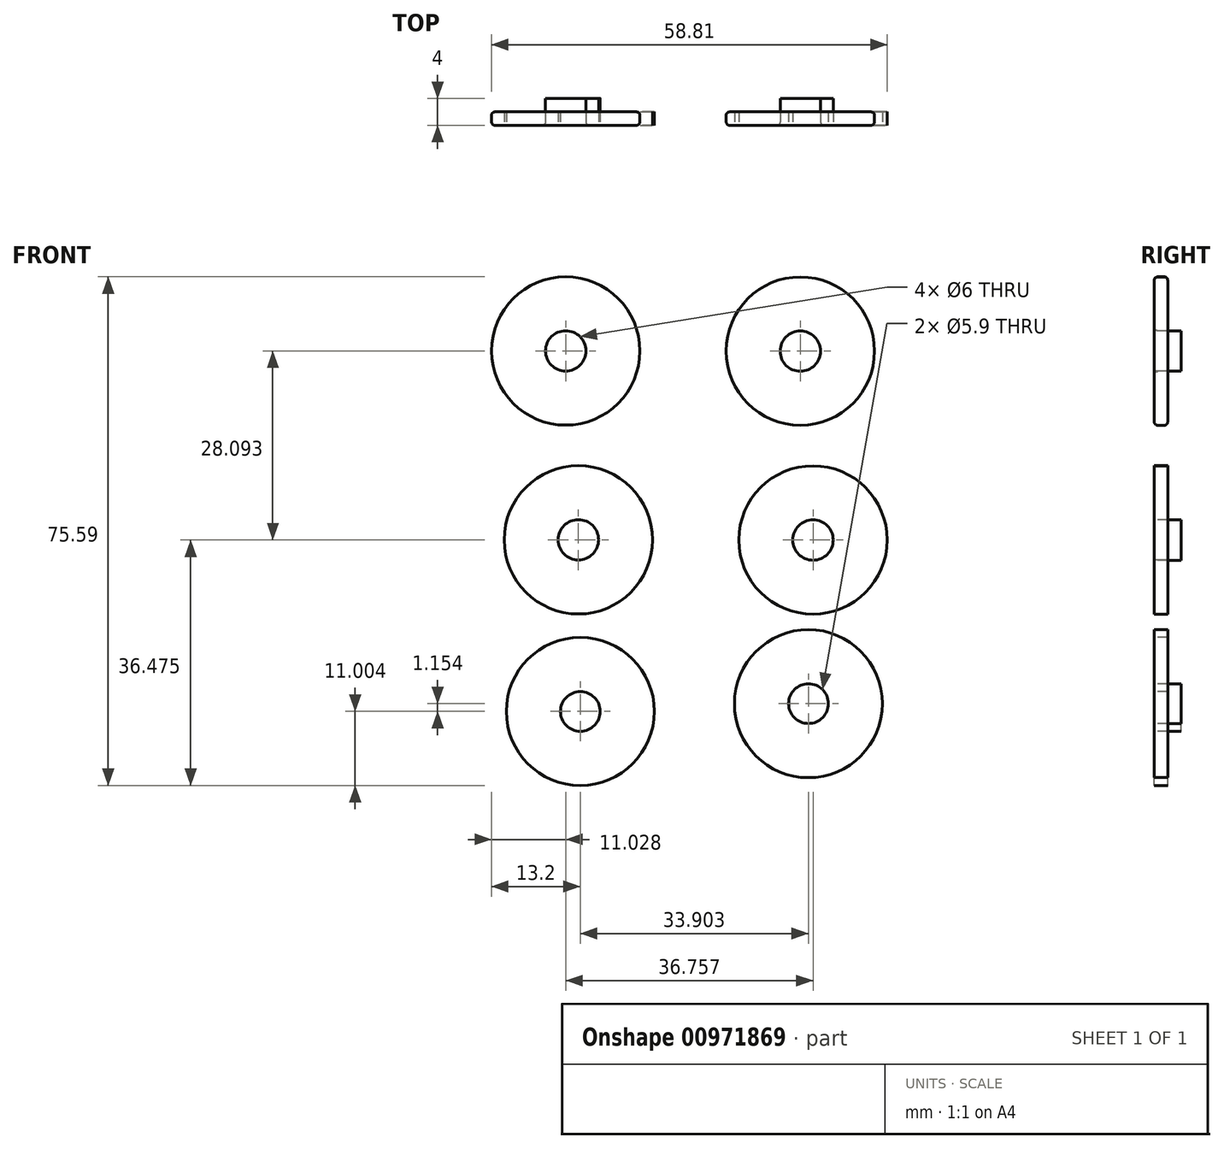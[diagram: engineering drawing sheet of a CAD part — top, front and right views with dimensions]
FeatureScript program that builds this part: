
annotation { "Feature Type Name" : "Feature", "Feature Type Description" : "" }
export const myFeature = defineFeature(function(context is Context, id is Id, definition is map)
    precondition{}
    {
        {
            var Q0;
            Q0=qCreatedBy(makeId("Front.planeOp"),FACE);
            var sketch = newSketch(context, id + "F0", { "sketchPlane" : qUnion([Q0])});
            skCircle(sketch, "E0", {"center": v(-13.67, 28.07) * mm, "radius": 11.03 * mm});
            skCircle(sketch, "E1", {"center": v(21.2, 28.04) * mm, "radius": 11.03 * mm});
            skCircle(sketch, "E2", {"center": v(-13.67, 28.07) * mm, "radius": 3 * mm});
            skCircle(sketch, "E3", {"center": v(21.2, 28.04) * mm, "radius": 3 * mm});
            skCircle(sketch, "E4", {"center": v(-11.79, 0) * mm, "radius": 11.03 * mm});
            skCircle(sketch, "E5", {"center": v(23.08, -0.02) * mm, "radius": 11.03 * mm});
            skCircle(sketch, "E6", {"center": v(-11.79, 0) * mm, "radius": 3 * mm});
            skCircle(sketch, "E7", {"center": v(23.08, -0.02) * mm, "radius": 3 * mm});
            skSolve(sketch);
        }
        {
            var Q0;
            Q0=makeQuery(id+"F0.imprint","IMPRINT",FACE,{"disambiguationData":[TD([[makeQuery(id+"F0.imprint","IMPRINT",EDGE,{"derivedFrom":sQuery(id+"F0.wireOp",EDGE,"E1")}),1.0]])]});
            var Q1;
            Q1=makeQuery(id+"F0.imprint","IMPRINT",FACE,{"disambiguationData":[TD([[makeQuery(id+"F0.imprint","IMPRINT",EDGE,{"derivedFrom":sQuery(id+"F0.wireOp",EDGE,"E0")}),1.0]])]});
            extrude(context, id + "F1", {"entities" : qUnion([Q0, Q1]), "depth" : -2 * mm, "offsetDistance" : 25.4 * mm});
        }
        {
            var Q0;
            Q0=makeQuery(id+"F1.opExtrude","CAP_EDGE",EDGE,{"disambiguationData":[OSD([sQuery(id+"F0.wireOp",EDGE,"E1")])],"isStart":false});
            var Q1;
            Q1=makeQuery(id+"F1.opExtrude","CAP_EDGE",EDGE,{"disambiguationData":[OSD([sQuery(id+"F0.wireOp",EDGE,"E0")])],"isStart":false});
            fillet(context, id + "F2", {"entities" : qUnion([Q0, Q1]), "radius" : .5 * mm, "tangentPropagation" : true, "allowEdgeOverflow" : false});
        }
        {
            var Q0;
            Q0=makeQuery(id+"F0.imprint","IMPRINT",FACE,{"disambiguationData":[TD([[makeQuery(id+"F0.imprint","IMPRINT",EDGE,{"derivedFrom":sQuery(id+"F0.wireOp",EDGE,"E2")}),1.0]])]});
            var Q1;
            Q1=makeQuery(id+"F0.imprint","IMPRINT",FACE,{"disambiguationData":[TD([[makeQuery(id+"F0.imprint","IMPRINT",EDGE,{"derivedFrom":sQuery(id+"F0.wireOp",EDGE,"E3")}),1.0]])]});
            extrude(context, id + "F3", {"entities" : qUnion([Q0, Q1]), "depth" : -4 * mm, "offsetDistance" : 25.4 * mm});
        }
        {
            var Q0;
            Q0=makeQuery(id+"F1.opExtrude","CAP_FACE",FACE,{"disambiguationData":[OSD([sQuery(id+"F0.wireOp",EDGE,"E0"),sQuery(id+"F0.wireOp",EDGE,"E2")])],"isStart":true});
            var Q1;
            Q1=makeQuery(id+"F1.opExtrude","CAP_FACE",FACE,{"disambiguationData":[OSD([sQuery(id+"F0.wireOp",EDGE,"E1"),sQuery(id+"F0.wireOp",EDGE,"E3")])],"isStart":true});
            fillet(context, id + "F4", {"entities" : qUnion([Q0, Q1]), "radius" : .55 * mm, "tangentPropagation" : true, "allowEdgeOverflow" : false});
        }
        {
            var Q0;
            Q0=makeQuery(id+"F0.imprint","IMPRINT",FACE,{"disambiguationData":[TD([[makeQuery(id+"F0.imprint","IMPRINT",EDGE,{"derivedFrom":sQuery(id+"F0.wireOp",EDGE,"E4")}),1.0]])]});
            var Q1;
            Q1=makeQuery(id+"F0.imprint","IMPRINT",FACE,{"disambiguationData":[TD([[makeQuery(id+"F0.imprint","IMPRINT",EDGE,{"derivedFrom":sQuery(id+"F0.wireOp",EDGE,"E5")}),1.0]])]});
            extrude(context, id + "F5", {"entities" : qUnion([Q0, Q1]), "depth" : -2 * mm, "offsetDistance" : 25 * mm});
        }
        {
            var Q0;
            Q0=makeQuery(id+"F0.imprint","IMPRINT",FACE,{"disambiguationData":[TD([[makeQuery(id+"F0.imprint","IMPRINT",EDGE,{"derivedFrom":sQuery(id+"F0.wireOp",EDGE,"E6")}),1.0]])]});
            var Q1;
            Q1=makeQuery(id+"F0.imprint","IMPRINT",FACE,{"disambiguationData":[TD([[makeQuery(id+"F0.imprint","IMPRINT",EDGE,{"derivedFrom":sQuery(id+"F0.wireOp",EDGE,"E7")}),1.0]])]});
            extrude(context, id + "F6", {"entities" : qUnion([Q0, Q1]), "depth" : -4 * mm, "offsetDistance" : 25 * mm});
        }
        {
            var Q0;
            Q0=qCreatedBy(makeId("Front.planeOp"),FACE);
            var sketch = newSketch(context, id + "F7", { "sketchPlane" : qUnion([Q0])});
            skCircle(sketch, "E8", {"center": v(22.4, -24.34) * mm, "radius": 11 * mm});
            skCircle(sketch, "E9", {"center": v(22.4, -24.34) * mm, "radius": 2.95 * mm});
            skCircle(sketch, "E10", {"center": v(-11.5, -25.5) * mm, "radius": 11 * mm});
            skCircle(sketch, "E11", {"center": v(-11.5, -25.5) * mm, "radius": 2.95 * mm});
            skSolve(sketch);
        }
        {
            var Q0;
            Q0=makeQuery(id+"F7.imprint","IMPRINT",FACE,{"disambiguationData":[TD([[makeQuery(id+"F7.imprint","IMPRINT",EDGE,{"derivedFrom":sQuery(id+"F7.wireOp",EDGE,"E10")}),1.0]])]});
            var Q1;
            Q1=makeQuery(id+"F7.imprint","IMPRINT",FACE,{"disambiguationData":[TD([[makeQuery(id+"F7.imprint","IMPRINT",EDGE,{"derivedFrom":sQuery(id+"F7.wireOp",EDGE,"E8")}),1.0]])]});
            extrude(context, id + "F8", {"entities" : qUnion([Q0, Q1]), "depth" : -2 * mm, "offsetDistance" : 25 * mm});
        }
        {
            var Q0;
            Q0=makeQuery(id+"F7.imprint","IMPRINT",FACE,{"disambiguationData":[TD([[makeQuery(id+"F7.imprint","IMPRINT",EDGE,{"derivedFrom":sQuery(id+"F7.wireOp",EDGE,"E11")}),1.0]])]});
            var Q1;
            Q1=makeQuery(id+"F7.imprint","IMPRINT",FACE,{"disambiguationData":[TD([[makeQuery(id+"F7.imprint","IMPRINT",EDGE,{"derivedFrom":sQuery(id+"F7.wireOp",EDGE,"E9")}),1.0]])]});
            extrude(context, id + "F9", {"entities" : qUnion([Q0, Q1]), "depth" : -4 * mm, "offsetDistance" : 25 * mm});
        }
    });
